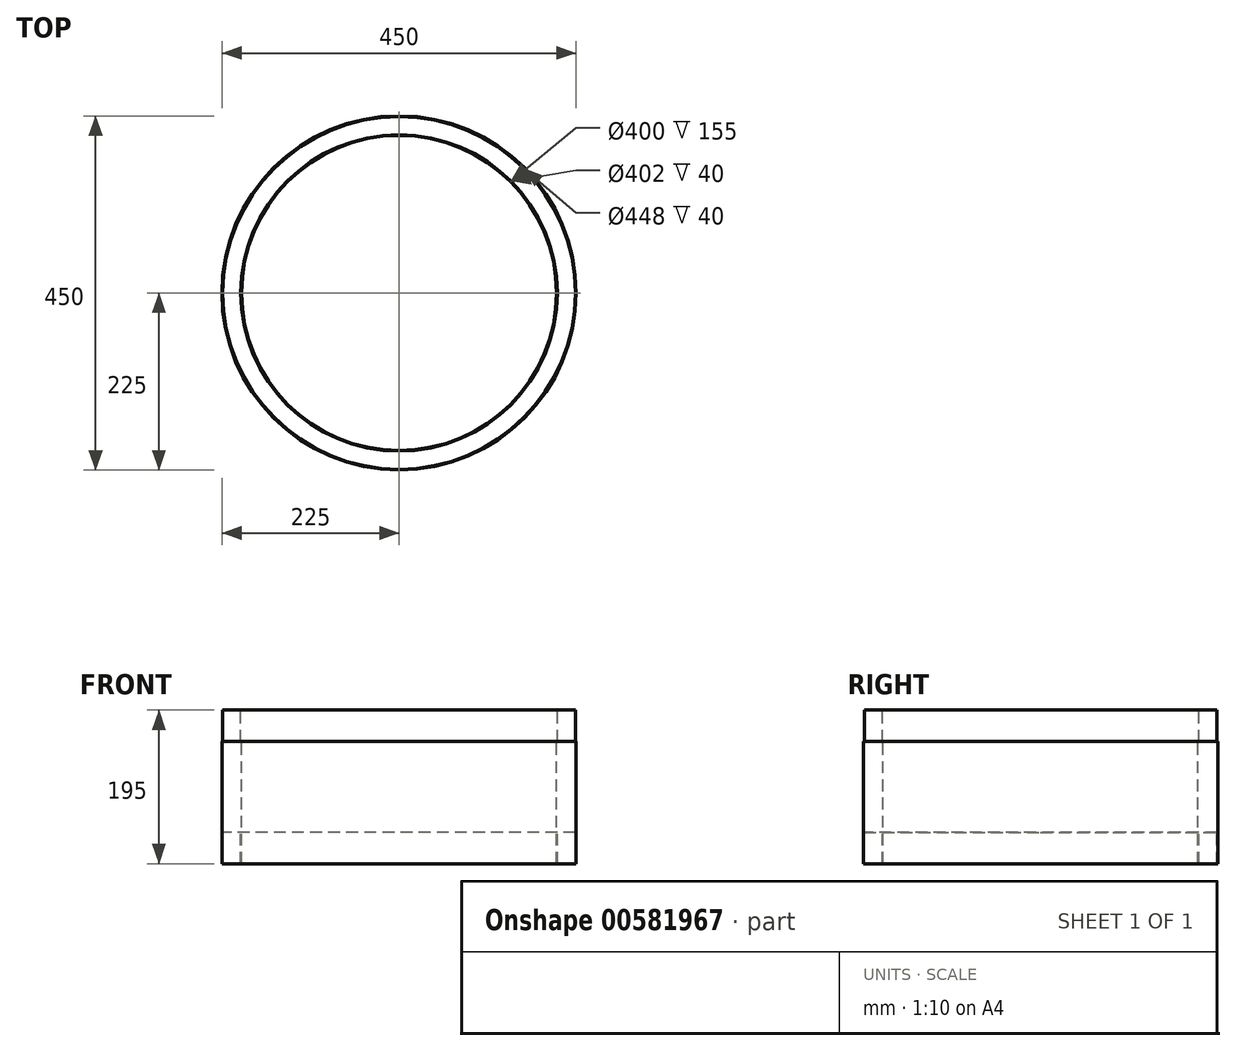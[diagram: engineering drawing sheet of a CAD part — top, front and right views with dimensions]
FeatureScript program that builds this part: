
annotation { "Feature Type Name" : "Feature", "Feature Type Description" : "" }
export const myFeature = defineFeature(function(context is Context, id is Id, definition is map)
    precondition{}
    {
        {
            var Q0;
            Q0=qCreatedBy(makeId("Front.planeOp"),FACE);
            var sketch = newSketch(context, id + "F0", { "sketchPlane" : qUnion([Q0])});
            skLineSegment(sketch, "E0", {"start": v(0, 345.75) * mm, "end": v(0, -558.03) * mm, "construction": true});
            skLineSegment(sketch, "E1", {"start": v(-200, -518.84) * mm, "end": v(-200, -363.84) * mm});
            skLineSegment(sketch, "E2", {"start": v(-200, -363.84) * mm, "end": v(-201, -363.84) * mm});
            skLineSegment(sketch, "E3", {"start": v(-201, -363.84) * mm, "end": v(-201, -323.84) * mm});
            skLineSegment(sketch, "E4", {"start": v(-201, -323.84) * mm, "end": v(-224, -323.84) * mm});
            skLineSegment(sketch, "E5", {"start": v(-224, -323.84) * mm, "end": v(-224, -363.84) * mm});
            skLineSegment(sketch, "E6", {"start": v(-224, -363.84) * mm, "end": v(-225, -363.84) * mm});
            skLineSegment(sketch, "E7", {"start": v(-225, -363.84) * mm, "end": v(-225, -518.84) * mm});
            skLineSegment(sketch, "E8", {"start": v(-225, -518.84) * mm, "end": v(-224, -518.84) * mm});
            skLineSegment(sketch, "E9", {"start": v(-224, -518.84) * mm, "end": v(-224, -478.84) * mm});
            skLineSegment(sketch, "E10", {"start": v(-224, -478.84) * mm, "end": v(-201, -478.84) * mm});
            skLineSegment(sketch, "E11", {"start": v(-201, -478.84) * mm, "end": v(-201, -518.84) * mm});
            skLineSegment(sketch, "E12", {"start": v(-201, -518.84) * mm, "end": v(-200, -518.84) * mm});
            skSolve(sketch);
        }
        {
            var Q0;
            Q0=qSketchRegion(id+"F0",true);
            var Q1;
            Q1=sQuery(id+"F0.wireOp",EDGE,"E0");
            revolve(context, id + "F1", {"entities" : qUnion([Q0]), "axis" : qUnion([Q1]), "revolveType" : RevolveType.FULL});
        }
    });
